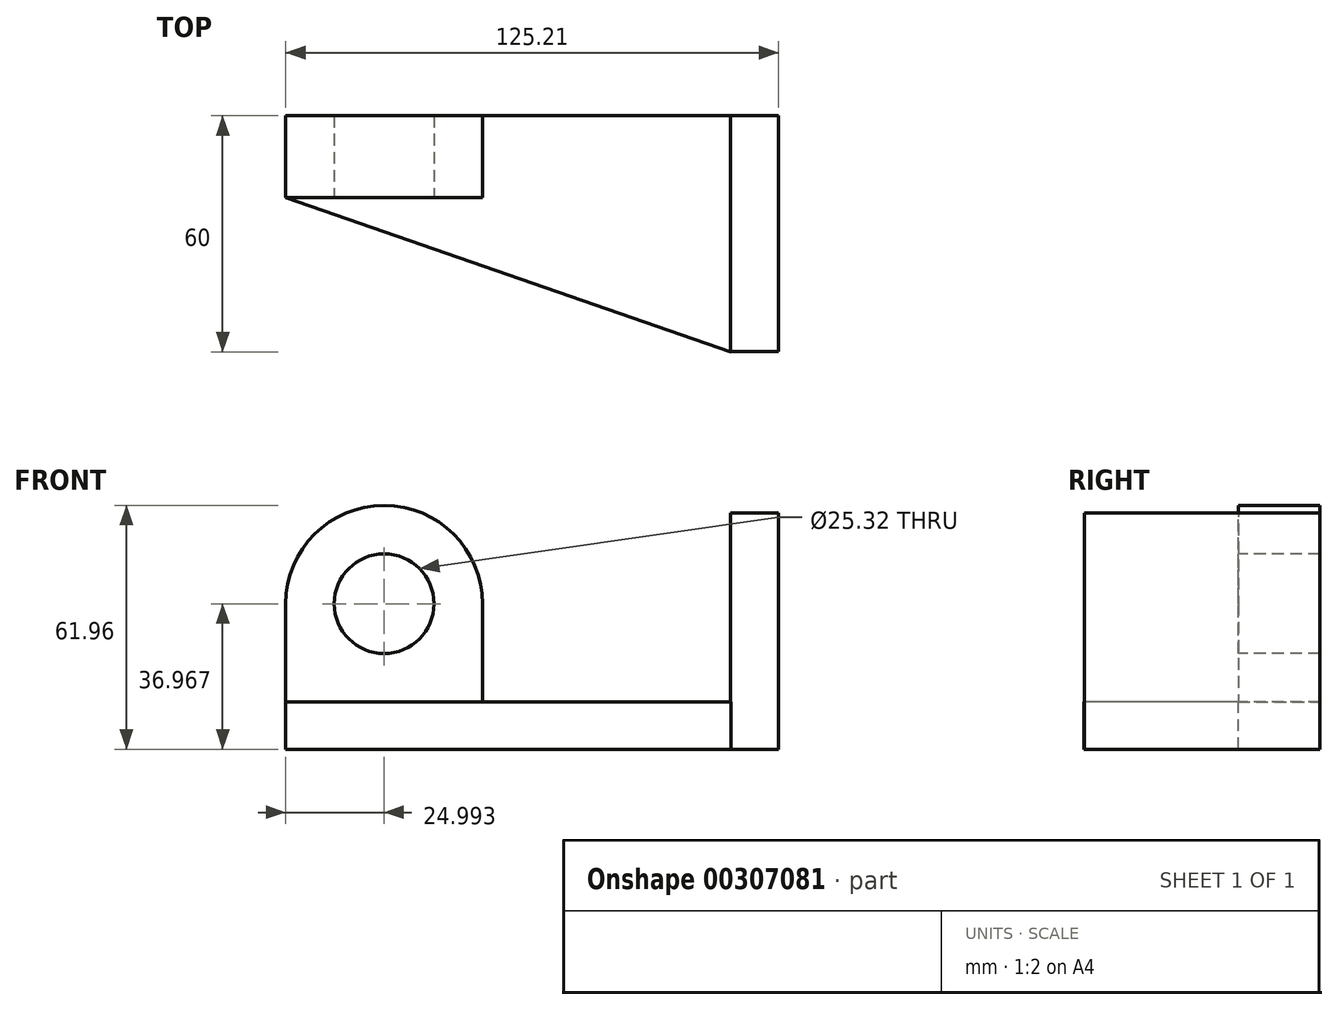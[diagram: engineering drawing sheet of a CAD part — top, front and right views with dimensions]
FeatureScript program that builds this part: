
annotation { "Feature Type Name" : "Feature", "Feature Type Description" : "" }
export const myFeature = defineFeature(function(context is Context, id is Id, definition is map)
    precondition{}
    {
        {
            var Q0;
            Q0=qCreatedBy(makeId("Front.planeOp"),FACE);
            var sketch = newSketch(context, id + "F0", { "sketchPlane" : qUnion([Q0])});
            skLineSegment(sketch, "E0.bottom", {"start": v(-69.5, 0) * mm, "end": v(43.57, 0) * mm});
            skLineSegment(sketch, "E0.top", {"start": v(-69.5, 11.97) * mm, "end": v(43.57, 11.97) * mm});
            skLineSegment(sketch, "E0.left", {"start": v(-69.5, 0) * mm, "end": v(-69.5, 11.97) * mm});
            skLineSegment(sketch, "E0.right", {"start": v(43.57, 0) * mm, "end": v(43.57, 11.97) * mm});
            skSolve(sketch);
        }
        {
            var Q0;
            Q0=makeQuery(id+"F0.imprint","IMPRINT",FACE,{"disambiguationData":[TD([[makeQuery(id+"F0.imprint","IMPRINT",EDGE,{"derivedFrom":sQuery(id+"F0.wireOp",EDGE,"E0.bottom")}),1.0]])]});
            extrude(context, id + "F1", {"entities" : qUnion([Q0]), "depth" : 60 * mm});
        }
        {
            var Q0;
            Q0=makeQuery(id+"F1.opExtrude","SWEPT_FACE",FACE,{"disambiguationData":[OSD([sQuery(id+"F0.wireOp",EDGE,"E0.top")])]});
            var sketch = newSketch(context, id + "F2", { "sketchPlane" : qUnion([Q0])});
            skLineSegment(sketch, "E1", {"start": v(-69.5, 0) * mm, "end": v(-69.5, -20.8) * mm});
            skLineSegment(sketch, "E2", {"start": v(-69.5, -20.8) * mm, "end": v(43.57, -60) * mm});
            skSolve(sketch);
        }
        {
            var Q0;
            {var subQ0=sQuery(id+"F2.wireOp",EDGE,"E2");Q0=makeQuery(id+"F2.imprint","IMPRINT",FACE,{"disambiguationData":[TD([[makeQuery(id+"F2.imprint","IMPRINT",EDGE,{"derivedFrom":subQ0}),-1.0]])]});}
            extrude(context, id + "F3", {"entities" : qUnion([Q0]), "operationType" : NewBodyOperationType.REMOVE, "oppositeDirection" : true, "depth" : 12 * mm});
        }
        {
            var Q0;
            Q0=makeQuery(id+"F1.opExtrude","SWEPT_FACE",FACE,{"disambiguationData":[OSD([sQuery(id+"F0.wireOp",EDGE,"E0.top")])]});
            var sketch = newSketch(context, id + "F4", { "sketchPlane" : qUnion([Q0])});
            skLineSegment(sketch, "E3", {"start": v(-69.5, -20.8) * mm, "end": v(-19.53, -20.8) * mm});
            skLineSegment(sketch, "E4", {"start": v(-19.53, -20.8) * mm, "end": v(-19.53, 0) * mm});
            skSolve(sketch);
        }
        {
            var Q0;
            Q0=qCreatedBy(makeId("Top.planeOp"),FACE);
            var sketch = newSketch(context, id + "F5", { "sketchPlane" : qUnion([Q0])});
            skLineSegment(sketch, "E5.bottom", {"start": v(43.54, -59.86) * mm, "end": v(55.7, -59.86) * mm});
            skLineSegment(sketch, "E5.top", {"start": v(43.54, 0) * mm, "end": v(55.7, 0) * mm});
            skLineSegment(sketch, "E5.left", {"start": v(43.54, -59.86) * mm, "end": v(43.54, 0) * mm});
            skLineSegment(sketch, "E5.right", {"start": v(55.7, -59.86) * mm, "end": v(55.7, 0) * mm});
            skSolve(sketch);
        }
        {
            var Q0;
            Q0=makeQuery(id+"F5.imprint","IMPRINT",FACE,{"disambiguationData":[TD([[makeQuery(id+"F5.imprint","IMPRINT",EDGE,{"derivedFrom":sQuery(id+"F5.wireOp",EDGE,"E5.bottom")}),1.0]])]});
            extrude(context, id + "F6", {"entities" : qUnion([Q0]), "operationType" : NewBodyOperationType.ADD, "depth" : 60 * mm});
        }
        {
            var Q0;
            Q0=makeQuery(id+"F4.imprint","IMPRINT",FACE,{"disambiguationData":[TD([[makeQuery(id+"F4.imprint","IMPRINT",EDGE,{"derivedFrom":sQuery(id+"F4.wireOp",EDGE,"E3")}),1.0]])]});
            extrude(context, id + "F7", {"entities" : qUnion([Q0]), "operationType" : NewBodyOperationType.ADD, "depth" : 50 * mm});
        }
        {
            var Q0;
            Q0=makeQuery(id+"F7.opExtrude","SWEPT_FACE",FACE,{"disambiguationData":[OSD([sQuery(id+"F4.wireOp",EDGE,"E3")])]});
            var sketch = newSketch(context, id + "F8", { "sketchPlane" : qUnion([Q0])});
            skCircle(sketch, "E6", {"center": v(-44.52, 36.97) * mm, "radius": 24.99 * mm});
            skPoint(sketch, "E6.centerSnap0", {"position": v(-69.5, 36.97) * mm});
            skPoint(sketch, "E6.centerSnap1", {"position": v(-44.52, 61.97) * mm});
            skSolve(sketch);
        }
        {
            var Q0;
            {var subQ1=sQuery(id+"F4.wireOp",EDGE,"E3");var subQ6=makeQuery(id+"F7.opExtrude","CAP_EDGE",EDGE,{"disambiguationData":[OSD([subQ1])],"isStart":false});Q0=makeQuery(id+"F8.imprint","IMPRINT",FACE,{"disambiguationData":[TD([[makeQuery(id+"F8.imprint","IMPRINT",EDGE,{"derivedFrom":subQ6}),-1.0]])]});}
            extrude(context, id + "F9", {"entities" : qUnion([Q0]), "operationType" : NewBodyOperationType.REMOVE, "oppositeDirection" : true, "depth" : 21 * mm});
        }
        {
            var Q0;
            Q0=makeQuery(id+"F7.opExtrude","SWEPT_FACE",FACE,{"disambiguationData":[OSD([sQuery(id+"F4.wireOp",EDGE,"E3")])]});
            var sketch = newSketch(context, id + "F10", { "sketchPlane" : qUnion([Q0])});
            skCircle(sketch, "E7", {"center": v(-44.52, 36.97) * mm, "radius": 12.66 * mm});
            skSolve(sketch);
        }
        {
            var Q0;
            Q0=makeQuery(id+"F10.imprint","IMPRINT",FACE,{"disambiguationData":[TD([[makeQuery(id+"F10.imprint","IMPRINT",EDGE,{"derivedFrom":sQuery(id+"F10.wireOp",EDGE,"E7")}),1.0]])]});
            extrude(context, id + "F11", {"entities" : qUnion([Q0]), "operationType" : NewBodyOperationType.REMOVE, "oppositeDirection" : true, "depth" : 21 * mm});
        }
    });
